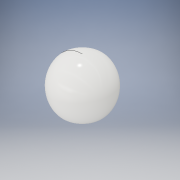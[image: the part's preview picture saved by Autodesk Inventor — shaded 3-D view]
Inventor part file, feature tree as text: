
AUTODESK INVENTOR PART (.ipt)
format: ipt  version: 2019 (Build 230136000, 136)  size: 239,616 bytes
history: native  units: in
note: dims shown in document units (in); Inventor stores cm internally (conversion verified against a paired STEP export)
features: other x1, shell x1
ambient origin geometry x8: Origin, YZ Plane, XZ Plane, XY Plane, X Axis, Y Axis, Z Axis, Center Point
bodies: Solid1 (feature_tree)
feature tree (2):
  other  "Form1"
  shell  "Shell1"  Thickness=0.15in
